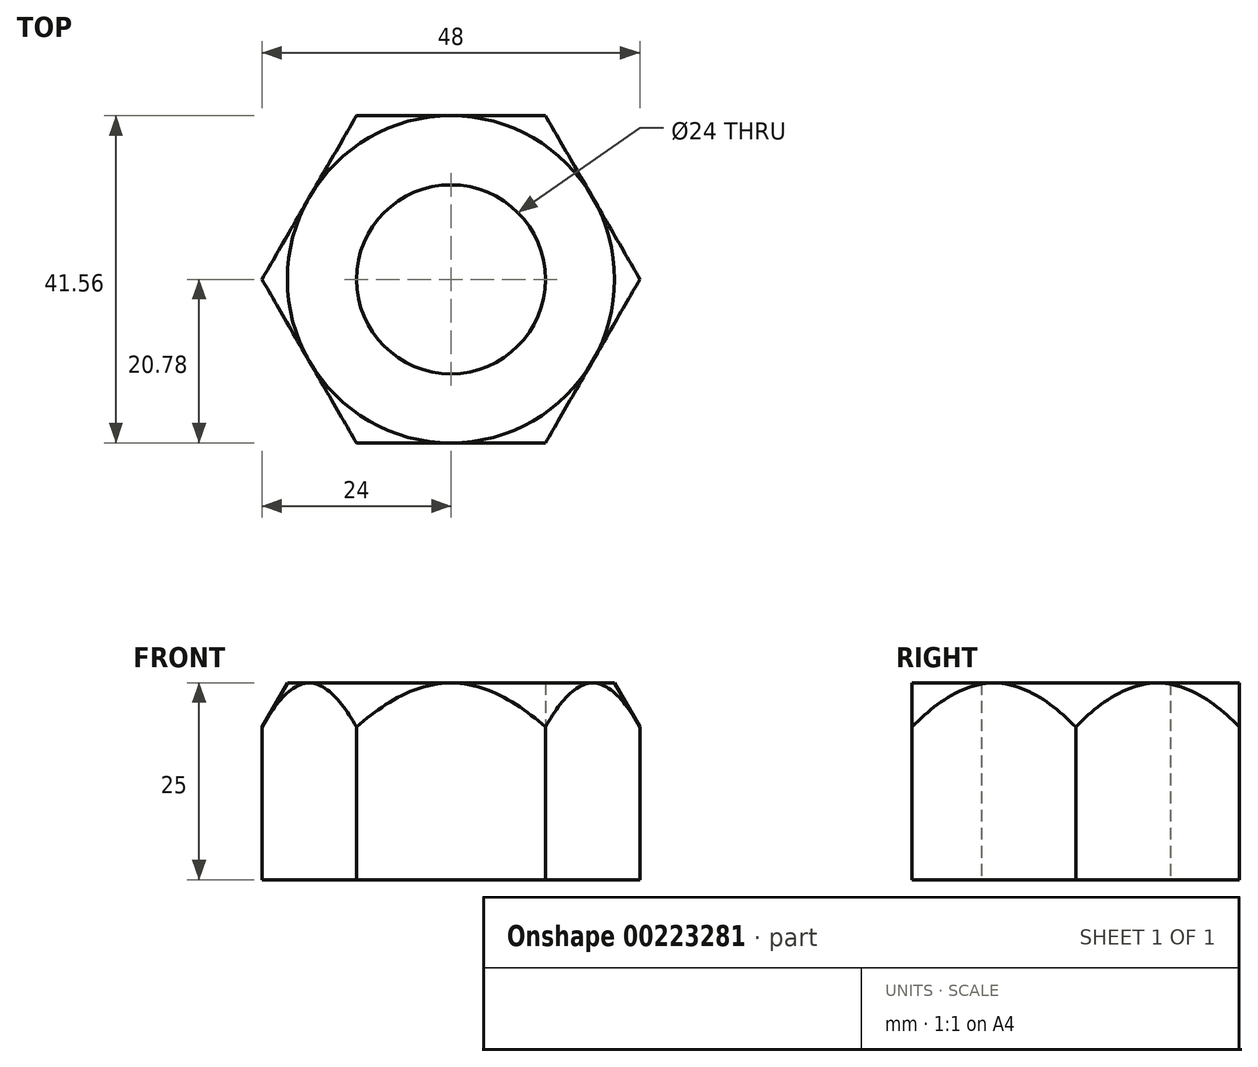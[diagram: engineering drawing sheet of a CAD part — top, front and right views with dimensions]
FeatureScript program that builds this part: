
annotation { "Feature Type Name" : "Feature", "Feature Type Description" : "" }
export const myFeature = defineFeature(function(context is Context, id is Id, definition is map)
    precondition{}
    {
        {
            var Q0;
            Q0=qCreatedBy(makeId("Top.planeOp"),FACE);
            var sketch = newSketch(context, id + "F0", { "sketchPlane" : qUnion([Q0])});
            skCircle(sketch, "E0.cCircle", {"center": v(0, 0) * mm, "radius": 20.78 * mm, "construction": true});
            skLineSegment(sketch, "E0.0", {"start": v(12, 20.78) * mm, "end": v(24, 0) * mm});
            skLineSegment(sketch, "E0.1", {"start": v(24, 0) * mm, "end": v(12, -20.78) * mm});
            skLineSegment(sketch, "E0.2", {"start": v(12, -20.78) * mm, "end": v(-12, -20.78) * mm});
            skLineSegment(sketch, "E0.3", {"start": v(-12, -20.78) * mm, "end": v(-24, 0) * mm});
            skLineSegment(sketch, "E0.4", {"start": v(-24, 0) * mm, "end": v(-12, 20.78) * mm});
            skLineSegment(sketch, "E0.5", {"start": v(-12, 20.78) * mm, "end": v(12, 20.78) * mm});
            skPoint(sketch, "E0.0.midPoint", {"position": v(18, 10.4) * mm});
            skCircle(sketch, "E1", {"center": v(0, 0) * mm, "radius": 12 * mm});
            skSolve(sketch);
        }
        {
            var Q0;
            Q0 = qSketchRegion(id + "F0", true);
            extrude(context, id + "F1", {"entities" : qUnion([Q0]), "depth" : 25 * mm});
        }
        {
            var Q0;
            Q0=makeQuery(id+"F1.opExtrude","CAP_FACE",FACE,{"disambiguationData":[OSD([sQuery(id+"F0.wireOp",EDGE,"E0.0"),sQuery(id+"F0.wireOp",EDGE,"E0.1"),sQuery(id+"F0.wireOp",EDGE,"E0.2"),sQuery(id+"F0.wireOp",EDGE,"E0.3"),sQuery(id+"F0.wireOp",EDGE,"E0.4"),sQuery(id+"F0.wireOp",EDGE,"E0.5")])],"isStart":false});
            var sketch = newSketch(context, id + "F2", { "sketchPlane" : qUnion([Q0])});
            skCircle(sketch, "E2", {"center": v(0, 0) * mm, "radius": 20.78 * mm, "construction": true});
            skSolve(sketch);
        }
        {
            var Q0;
            Q0=qCreatedBy(makeId("Front.planeOp"),FACE);
            var sketch = newSketch(context, id + "F3", { "sketchPlane" : qUnion([Q0])});
            skLineSegment(sketch, "E3.0", {"start": v(-20.78, 25) * mm, "end": v(20.78, 25) * mm, "construction": true});
            skLineSegment(sketch, "E4", {"start": v(20.78, 25) * mm, "end": v(24, 25) * mm});
            skLineSegment(sketch, "E5", {"start": v(24, 25) * mm, "end": v(24, 19.43) * mm});
            skLineSegment(sketch, "E6", {"start": v(24, 19.43) * mm, "end": v(20.78, 25) * mm});
            skLineSegment(sketch, "E7", {"start": v(0, -13.25) * mm, "end": v(0, 41.29) * mm});
            skSolve(sketch);
        }
        {
            var Q0;
            Q0 = qSketchRegion(id + "F3", true);
            var Q1;
            Q1=sQuery(id+"F3.wireOp",EDGE,"E7");
            revolve(context, id + "F4", {"operationType" : NewBodyOperationType.REMOVE, "entities" : qUnion([Q0]), "axis" : qUnion([Q1]), "revolveType" : RevolveType.FULL, "oppositeDirection" : true});
        }
    });
